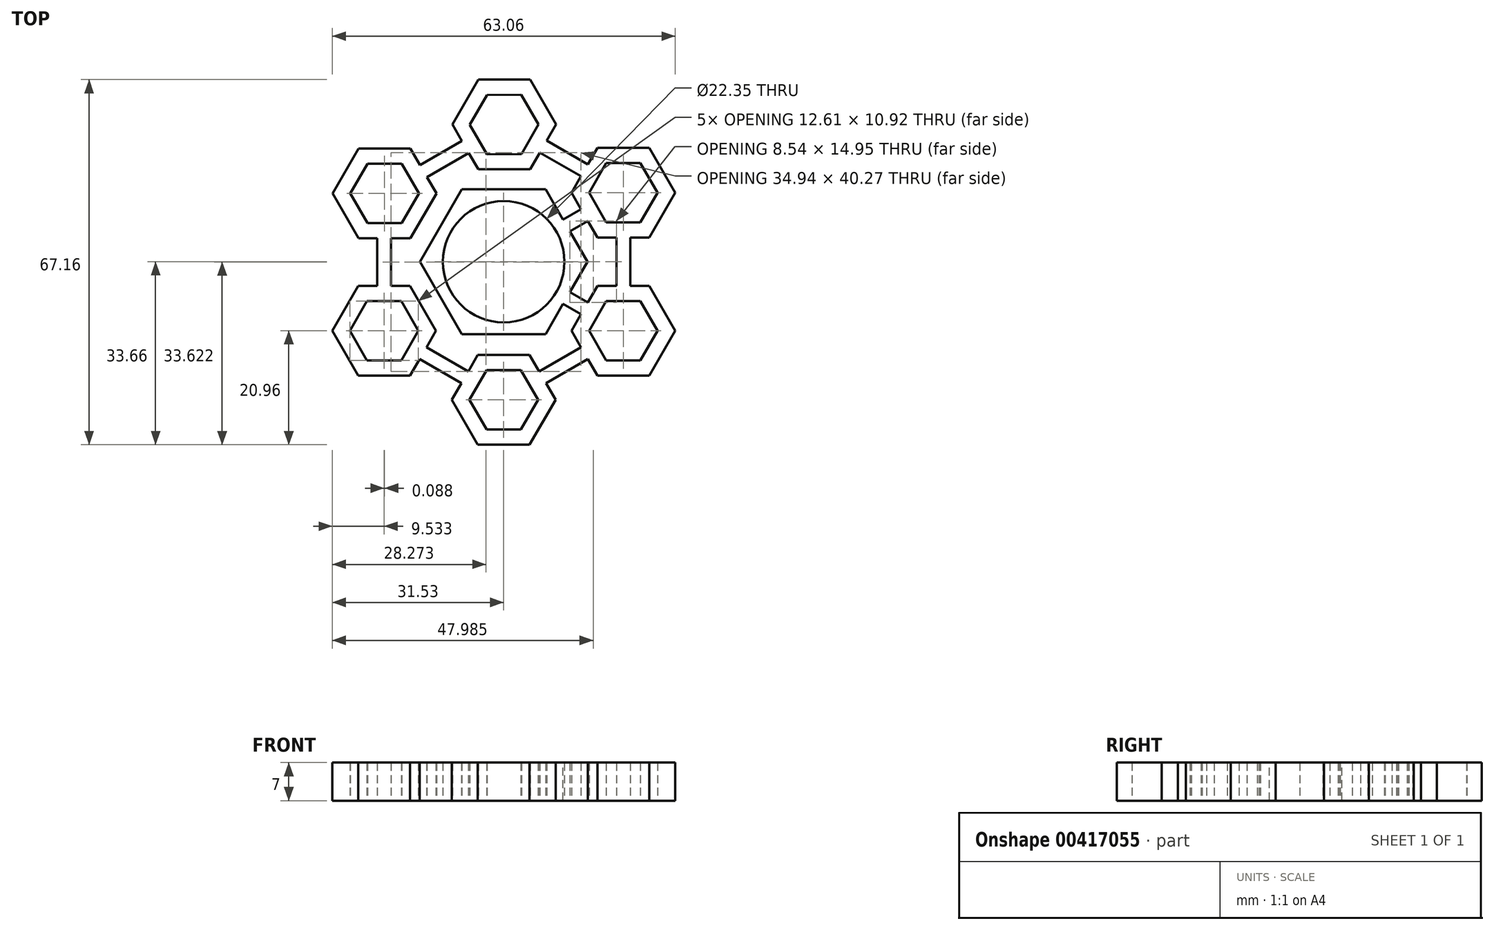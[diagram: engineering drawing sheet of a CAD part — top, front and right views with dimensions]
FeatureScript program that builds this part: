
annotation { "Feature Type Name" : "Feature", "Feature Type Description" : "" }
export const myFeature = defineFeature(function(context is Context, id is Id, definition is map)
    precondition{}
    {
        {
            var Q0;
            Q0=qCreatedBy(makeId("Top.planeOp"),FACE);
            var sketch = newSketch(context, id + "F0", { "sketchPlane" : qUnion([Q0])});
            skCircle(sketch, "E0", {"center": v(0, 0) * mm, "radius": 10.95 * mm});
            skCircle(sketch, "E1.cCircle", {"center": v(0, 0) * mm, "radius": 12.7 * mm, "construction": true});
            skLineSegment(sketch, "E1.0", {"start": v(-7.33, 12.7) * mm, "end": v(7.33, 12.7) * mm});
            skLineSegment(sketch, "E1.1", {"start": v(7.33, 12.7) * mm, "end": v(14.66, 0) * mm});
            skLineSegment(sketch, "E1.2", {"start": v(14.66, 0) * mm, "end": v(7.33, -12.7) * mm});
            skLineSegment(sketch, "E1.3", {"start": v(7.33, -12.7) * mm, "end": v(-7.33, -12.7) * mm});
            skLineSegment(sketch, "E1.4", {"start": v(-7.33, -12.7) * mm, "end": v(-14.66, 0) * mm});
            skLineSegment(sketch, "E1.5", {"start": v(-14.66, 0) * mm, "end": v(-7.33, 12.7) * mm});
            skPoint(sketch, "E1.0.midPoint", {"position": v(0, 12.7) * mm});
            skPoint(sketch, "E2.endSnap0", {"position": v(0, -12.7) * mm});
            skCircle(sketch, "E3.cCircle", {"center": v(0.09, 25.25) * mm, "radius": 5.46 * mm, "construction": true});
            skLineSegment(sketch, "E3.0", {"start": v(3.26, 19.8) * mm, "end": v(-3.05, 19.78) * mm});
            skLineSegment(sketch, "E3.1", {"start": v(-3.05, 19.78) * mm, "end": v(-6.22, 25.23) * mm});
            skLineSegment(sketch, "E3.2", {"start": v(-6.22, 25.23) * mm, "end": v(-3.08, 30.7) * mm});
            skLineSegment(sketch, "E3.3", {"start": v(-3.08, 30.7) * mm, "end": v(3.22, 30.72) * mm});
            skLineSegment(sketch, "E3.4", {"start": v(3.22, 30.72) * mm, "end": v(6.4, 25.27) * mm});
            skLineSegment(sketch, "E3.5", {"start": v(6.4, 25.27) * mm, "end": v(3.26, 19.8) * mm});
            skPoint(sketch, "E3.0.midPoint", {"position": v(0.1, 19.79) * mm});
            skCircle(sketch, "E4.cCircle", {"center": v(22, 12.7) * mm, "radius": 5.46 * mm, "construction": true});
            skLineSegment(sketch, "E4.0", {"start": v(18.84, 7.24) * mm, "end": v(15.7, 12.7) * mm});
            skLineSegment(sketch, "E4.1", {"start": v(15.7, 12.7) * mm, "end": v(18.84, 18.16) * mm});
            skLineSegment(sketch, "E4.2", {"start": v(18.84, 18.16) * mm, "end": v(25.15, 18.16) * mm});
            skLineSegment(sketch, "E4.3", {"start": v(25.15, 18.16) * mm, "end": v(28.3, 12.7) * mm});
            skLineSegment(sketch, "E4.4", {"start": v(28.3, 12.7) * mm, "end": v(25.15, 7.24) * mm});
            skLineSegment(sketch, "E4.5", {"start": v(25.15, 7.24) * mm, "end": v(18.84, 7.24) * mm});
            skPoint(sketch, "E4.0.midPoint", {"position": v(17.27, 9.97) * mm});
            skCircle(sketch, "E5.cCircle", {"center": v(22, -12.7) * mm, "radius": 5.46 * mm, "construction": true});
            skLineSegment(sketch, "E5.0", {"start": v(15.7, -12.7) * mm, "end": v(18.84, -7.24) * mm});
            skLineSegment(sketch, "E5.1", {"start": v(18.84, -7.24) * mm, "end": v(25.15, -7.24) * mm});
            skLineSegment(sketch, "E5.2", {"start": v(25.15, -7.24) * mm, "end": v(28.3, -12.7) * mm});
            skLineSegment(sketch, "E5.3", {"start": v(28.3, -12.7) * mm, "end": v(25.15, -18.16) * mm});
            skLineSegment(sketch, "E5.4", {"start": v(25.15, -18.16) * mm, "end": v(18.84, -18.16) * mm});
            skLineSegment(sketch, "E5.5", {"start": v(18.84, -18.16) * mm, "end": v(15.7, -12.7) * mm});
            skPoint(sketch, "E5.0.midPoint", {"position": v(17.27, -9.97) * mm});
            skCircle(sketch, "E6.cCircle", {"center": v(0, -25.4) * mm, "radius": 5.46 * mm, "construction": true});
            skLineSegment(sketch, "E6.0", {"start": v(-3.15, -19.94) * mm, "end": v(3.15, -19.94) * mm});
            skLineSegment(sketch, "E6.1", {"start": v(3.15, -19.94) * mm, "end": v(6.3, -25.4) * mm});
            skLineSegment(sketch, "E6.2", {"start": v(6.3, -25.4) * mm, "end": v(3.15, -30.86) * mm});
            skLineSegment(sketch, "E6.3", {"start": v(3.15, -30.86) * mm, "end": v(-3.15, -30.86) * mm});
            skLineSegment(sketch, "E6.4", {"start": v(-3.15, -30.86) * mm, "end": v(-6.3, -25.4) * mm});
            skLineSegment(sketch, "E6.5", {"start": v(-6.3, -25.4) * mm, "end": v(-3.15, -19.94) * mm});
            skPoint(sketch, "E6.0.midPoint", {"position": v(0, -19.94) * mm});
            skCircle(sketch, "E7.cCircle", {"center": v(-22, -12.7) * mm, "radius": 5.46 * mm, "construction": true});
            skLineSegment(sketch, "E7.0", {"start": v(-18.84, -7.24) * mm, "end": v(-15.7, -12.7) * mm});
            skLineSegment(sketch, "E7.1", {"start": v(-15.7, -12.7) * mm, "end": v(-18.84, -18.16) * mm});
            skLineSegment(sketch, "E7.2", {"start": v(-18.84, -18.16) * mm, "end": v(-25.15, -18.16) * mm});
            skLineSegment(sketch, "E7.3", {"start": v(-25.15, -18.16) * mm, "end": v(-28.3, -12.7) * mm});
            skLineSegment(sketch, "E7.4", {"start": v(-28.3, -12.7) * mm, "end": v(-25.15, -7.24) * mm});
            skLineSegment(sketch, "E7.5", {"start": v(-25.15, -7.24) * mm, "end": v(-18.84, -7.24) * mm});
            skPoint(sketch, "E7.0.midPoint", {"position": v(-17.27, -9.97) * mm});
            skCircle(sketch, "E8.cCircle", {"center": v(-21.9, 12.55) * mm, "radius": 5.46 * mm, "construction": true});
            skLineSegment(sketch, "E8.0", {"start": v(-15.6, 12.55) * mm, "end": v(-18.76, 7.09) * mm});
            skLineSegment(sketch, "E8.1", {"start": v(-18.76, 7.09) * mm, "end": v(-25.06, 7.09) * mm});
            skLineSegment(sketch, "E8.2", {"start": v(-25.06, 7.09) * mm, "end": v(-28.21, 12.55) * mm});
            skLineSegment(sketch, "E8.3", {"start": v(-28.21, 12.55) * mm, "end": v(-25.06, 18) * mm});
            skLineSegment(sketch, "E8.4", {"start": v(-25.06, 18) * mm, "end": v(-18.76, 18) * mm});
            skLineSegment(sketch, "E8.5", {"start": v(-18.76, 18) * mm, "end": v(-15.6, 12.55) * mm});
            skPoint(sketch, "E8.0.midPoint", {"position": v(-17.18, 9.82) * mm});
            skCircle(sketch, "E9.cCircle", {"center": v(-21.9, 12.55) * mm, "radius": 8.26 * mm, "construction": true});
            skLineSegment(sketch, "E9.0", {"start": v(-12.38, 12.55) * mm, "end": v(-17.14, 4.3) * mm});
            skLineSegment(sketch, "E9.1", {"start": v(-17.14, 4.3) * mm, "end": v(-26.67, 4.3) * mm});
            skLineSegment(sketch, "E9.2", {"start": v(-26.67, 4.3) * mm, "end": v(-31.44, 12.55) * mm});
            skLineSegment(sketch, "E9.3", {"start": v(-31.44, 12.55) * mm, "end": v(-26.67, 20.8) * mm});
            skLineSegment(sketch, "E9.4", {"start": v(-26.67, 20.8) * mm, "end": v(-17.14, 20.8) * mm});
            skLineSegment(sketch, "E9.5", {"start": v(-17.14, 20.8) * mm, "end": v(-12.38, 12.55) * mm});
            skPoint(sketch, "E9.0.midPoint", {"position": v(-14.76, 8.42) * mm});
            skCircle(sketch, "E10.cCircle", {"center": v(0.09, 25.25) * mm, "radius": 8.26 * mm, "construction": true});
            skLineSegment(sketch, "E10.0", {"start": v(4.85, 17) * mm, "end": v(-4.68, 17) * mm});
            skLineSegment(sketch, "E10.1", {"start": v(-4.68, 17) * mm, "end": v(-9.44, 25.25) * mm});
            skLineSegment(sketch, "E10.2", {"start": v(-9.44, 25.25) * mm, "end": v(-4.68, 33.5) * mm});
            skLineSegment(sketch, "E10.3", {"start": v(-4.68, 33.5) * mm, "end": v(4.85, 33.5) * mm});
            skLineSegment(sketch, "E10.4", {"start": v(4.85, 33.5) * mm, "end": v(9.62, 25.25) * mm});
            skLineSegment(sketch, "E10.5", {"start": v(9.62, 25.25) * mm, "end": v(4.85, 17) * mm});
            skPoint(sketch, "E10.0.midPoint", {"position": v(0.09, 17) * mm});
            skCircle(sketch, "E11.cCircle", {"center": v(22, 12.7) * mm, "radius": 8.26 * mm, "construction": true});
            skLineSegment(sketch, "E11.0", {"start": v(17.23, 4.45) * mm, "end": v(12.46, 12.7) * mm});
            skLineSegment(sketch, "E11.1", {"start": v(12.46, 12.7) * mm, "end": v(17.23, 20.96) * mm});
            skLineSegment(sketch, "E11.2", {"start": v(17.23, 20.96) * mm, "end": v(26.76, 20.96) * mm});
            skLineSegment(sketch, "E11.3", {"start": v(26.76, 20.96) * mm, "end": v(31.53, 12.7) * mm});
            skLineSegment(sketch, "E11.4", {"start": v(31.53, 12.7) * mm, "end": v(26.76, 4.45) * mm});
            skLineSegment(sketch, "E11.5", {"start": v(26.76, 4.45) * mm, "end": v(17.23, 4.45) * mm});
            skPoint(sketch, "E11.0.midPoint", {"position": v(14.85, 8.57) * mm});
            skCircle(sketch, "E12.cCircle", {"center": v(22, -12.7) * mm, "radius": 8.26 * mm, "construction": true});
            skLineSegment(sketch, "E12.0", {"start": v(12.46, -12.7) * mm, "end": v(17.23, -4.44) * mm});
            skLineSegment(sketch, "E12.1", {"start": v(17.23, -4.45) * mm, "end": v(26.76, -4.44) * mm});
            skLineSegment(sketch, "E12.2", {"start": v(26.76, -4.44) * mm, "end": v(31.53, -12.7) * mm});
            skLineSegment(sketch, "E12.3", {"start": v(31.53, -12.7) * mm, "end": v(26.76, -20.96) * mm});
            skLineSegment(sketch, "E12.4", {"start": v(26.76, -20.96) * mm, "end": v(17.23, -20.96) * mm});
            skLineSegment(sketch, "E12.5", {"start": v(17.23, -20.96) * mm, "end": v(12.46, -12.7) * mm});
            skPoint(sketch, "E12.0.midPoint", {"position": v(14.85, -8.57) * mm});
            skCircle(sketch, "E13.cCircle", {"center": v(0, -25.4) * mm, "radius": 8.26 * mm, "construction": true});
            skLineSegment(sketch, "E13.0", {"start": v(-4.77, -17.14) * mm, "end": v(4.77, -17.14) * mm});
            skLineSegment(sketch, "E13.1", {"start": v(4.77, -17.15) * mm, "end": v(9.53, -25.4) * mm});
            skLineSegment(sketch, "E13.2", {"start": v(9.53, -25.4) * mm, "end": v(4.77, -33.65) * mm});
            skLineSegment(sketch, "E13.3", {"start": v(4.77, -33.65) * mm, "end": v(-4.77, -33.66) * mm});
            skLineSegment(sketch, "E13.4", {"start": v(-4.77, -33.66) * mm, "end": v(-9.53, -25.4) * mm});
            skLineSegment(sketch, "E13.5", {"start": v(-9.53, -25.4) * mm, "end": v(-4.77, -17.15) * mm});
            skPoint(sketch, "E13.0.midPoint", {"position": v(0, -17.14) * mm});
            skCircle(sketch, "E14.cCircle", {"center": v(-22, -12.7) * mm, "radius": 8.26 * mm, "construction": true});
            skLineSegment(sketch, "E14.0", {"start": v(-17.23, -4.45) * mm, "end": v(-12.46, -12.7) * mm});
            skLineSegment(sketch, "E14.1", {"start": v(-12.46, -12.7) * mm, "end": v(-17.23, -20.96) * mm});
            skLineSegment(sketch, "E14.2", {"start": v(-17.23, -20.96) * mm, "end": v(-26.76, -20.96) * mm});
            skLineSegment(sketch, "E14.3", {"start": v(-26.76, -20.96) * mm, "end": v(-31.53, -12.7) * mm});
            skLineSegment(sketch, "E14.4", {"start": v(-31.53, -12.7) * mm, "end": v(-26.76, -4.45) * mm});
            skLineSegment(sketch, "E14.5", {"start": v(-26.76, -4.45) * mm, "end": v(-17.23, -4.45) * mm});
            skPoint(sketch, "E14.0.midPoint", {"position": v(-14.85, -8.57) * mm});
            skLineSegment(sketch, "E15", {"start": v(-6.43, 20.02) * mm, "end": v(-14.12, 15.57) * mm});
            skLineSegment(sketch, "E16", {"start": v(-14.21, 15.73) * mm, "end": v(-15.4, 17.77) * mm});
            skLineSegment(sketch, "E17", {"start": v(-15.4, 17.77) * mm, "end": v(-7.7, 22.22) * mm});
            skLineSegment(sketch, "E18", {"start": v(-23.27, 4.3) * mm, "end": v(-23.27, -4.45) * mm});
            skLineSegment(sketch, "E19", {"start": v(-23.27, -4.45) * mm, "end": v(-20.73, -4.45) * mm});
            skLineSegment(sketch, "E20", {"start": v(-20.73, -4.45) * mm, "end": v(-20.73, 4.3) * mm});
            skLineSegment(sketch, "E21", {"start": v(-15.48, -17.93) * mm, "end": v(-7.78, -22.37) * mm});
            skLineSegment(sketch, "E22", {"start": v(-7.78, -22.37) * mm, "end": v(-6.51, -20.17) * mm});
            skLineSegment(sketch, "E23", {"start": v(-6.51, -20.17) * mm, "end": v(-14.21, -15.73) * mm});
            skLineSegment(sketch, "E24", {"start": v(6.51, -20.17) * mm, "end": v(14.21, -15.73) * mm});
            skLineSegment(sketch, "E25", {"start": v(14.21, -15.73) * mm, "end": v(15.48, -17.93) * mm});
            skLineSegment(sketch, "E26", {"start": v(15.48, -17.93) * mm, "end": v(7.7, -22.42) * mm});
            skLineSegment(sketch, "E27", {"start": v(20.73, -4.45) * mm, "end": v(20.73, 4.45) * mm});
            skLineSegment(sketch, "E28", {"start": v(20.73, 4.45) * mm, "end": v(23.27, 4.45) * mm});
            skLineSegment(sketch, "E29", {"start": v(23.27, 4.45) * mm, "end": v(23.27, -4.54) * mm});
            skLineSegment(sketch, "E30", {"start": v(14.21, 15.73) * mm, "end": v(6.65, 20.1) * mm});
            skLineSegment(sketch, "E31", {"start": v(6.65, 20.1) * mm, "end": v(7.92, 22.3) * mm});
            skLineSegment(sketch, "E32", {"start": v(7.92, 22.3) * mm, "end": v(15.48, 17.93) * mm});
            skLineSegment(sketch, "E33.bottom", {"start": v(-1.27, -12.7) * mm, "end": v(1.27, -12.7) * mm});
            skLineSegment(sketch, "E33.top", {"start": v(-1.27, -17.14) * mm, "end": v(1.27, -17.14) * mm});
            skLineSegment(sketch, "E34.bottom", {"start": v(1.27, 12.7) * mm, "end": v(-1.27, 12.7) * mm});
            skLineSegment(sketch, "E34.top", {"start": v(1.27, 17) * mm, "end": v(-1.27, 17) * mm});
            skLineSegment(sketch, "E35", {"start": v(14.21, 9.67) * mm, "end": v(10.3, 7.42) * mm});
            skLineSegment(sketch, "E36", {"start": v(10.3, 7.42) * mm, "end": v(11.63, 5.25) * mm});
            skLineSegment(sketch, "E37", {"start": v(11.63, 5.25) * mm, "end": v(15.48, 7.47) * mm});
            skLineSegment(sketch, "E38", {"start": v(15.48, -7.47) * mm, "end": v(11.58, -5.22) * mm});
            skLineSegment(sketch, "E39", {"start": v(11.58, -5.22) * mm, "end": v(10.36, -7.45) * mm});
            skLineSegment(sketch, "E40", {"start": v(10.36, -7.45) * mm, "end": v(14.21, -9.67) * mm});
            skLineSegment(sketch, "E41", {"start": v(-10.36, -7.45) * mm, "end": v(-14.21, -9.67) * mm});
            skLineSegment(sketch, "E42", {"start": v(-14.21, -9.67) * mm, "end": v(-15.48, -7.47) * mm});
            skLineSegment(sketch, "E43", {"start": v(-15.48, -7.47) * mm, "end": v(-11.63, -5.25) * mm});
            skLineSegment(sketch, "E44", {"start": v(-11.63, 5.25) * mm, "end": v(-15.35, 7.4) * mm});
            skLineSegment(sketch, "E45", {"start": v(-15.35, 7.4) * mm, "end": v(-14.08, 9.6) * mm});
            skLineSegment(sketch, "E46", {"start": v(-14.08, 9.6) * mm, "end": v(-10.36, 7.45) * mm});
            skLineSegment(sketch, "E47", {"start": v(-11.63, 5.25) * mm, "end": v(-10.36, 7.45) * mm});
            skLineSegment(sketch, "E48", {"start": v(-14.08, 9.6) * mm, "end": v(-15.35, 7.4) * mm});
            skLineSegment(sketch, "E49", {"start": v(15.48, 7.47) * mm, "end": v(14.21, 9.67) * mm});
            skLineSegment(sketch, "E50", {"start": v(-11.63, -5.25) * mm, "end": v(-15.48, -7.47) * mm});
            skLineSegment(sketch, "E51", {"start": v(-15.48, -7.47) * mm, "end": v(-14.21, -9.67) * mm});
            skLineSegment(sketch, "E52", {"start": v(-14.21, -9.67) * mm, "end": v(-10.36, -7.45) * mm});
            skLineSegment(sketch, "E53", {"start": v(-10.36, -7.45) * mm, "end": v(-11.63, -5.25) * mm});
            skCircle(sketch, "E54", {"center": v(0, 0) * mm, "radius": 11.08 * mm});
            skCircle(sketch, "E55", {"center": v(0, 0) * mm, "radius": 11.07 * mm});
            skSolve(sketch);
        }
        {
            var Q0;
            Q0 = qSketchRegion(id + "F0", true);
            var Q1;
            Q1=makeQuery(id+"F0.imprint","IMPRINT",FACE,{"disambiguationData":[TD([[makeQuery(id+"F0.imprint","IMPRINT",EDGE,{"derivedFrom":sQuery(id+"F0.wireOp",EDGE,"E34.bottom")}),-1.0]])]});
            var Q2;
            Q2=makeQuery(id+"F0.imprint","IMPRINT",FACE,{"disambiguationData":[TD([[makeQuery(id+"F0.imprint","IMPRINT",EDGE,{"derivedFrom":sQuery(id+"F0.wireOp",EDGE,"E50")}),1.0]])]});
            var Q3;
            Q3=makeQuery(id+"F0.imprint","IMPRINT",FACE,{"disambiguationData":[TD([[makeQuery(id+"F0.imprint","IMPRINT",EDGE,{"derivedFrom":sQuery(id+"F0.wireOp",EDGE,"E33.bottom")}),-1.0]])]});
            var Q4;
            {var subQ0=sQuery(id+"F0.wireOp",EDGE,"E40");Q4=makeQuery(id+"F0.imprint","IMPRINT",FACE,{"disambiguationData":[TD([[makeQuery(id+"F0.imprint","IMPRINT",EDGE,{"derivedFrom":subQ0}),1.0]])]});}
            var Q5;
            {var subQ0=sQuery(id+"F0.wireOp",EDGE,"E37");Q5=makeQuery(id+"F0.imprint","IMPRINT",FACE,{"disambiguationData":[TD([[makeQuery(id+"F0.imprint","IMPRINT",EDGE,{"derivedFrom":subQ0}),1.0]])]});}
            var Q6;
            Q6=makeQuery(id+"F0.imprint","IMPRINT",FACE,{"disambiguationData":[TD([[makeQuery(id+"F0.imprint","IMPRINT",EDGE,{"derivedFrom":sQuery(id+"F0.wireOp",EDGE,"E46")}),-1.0]])]});
            extrude(context, id + "F1", {"entities" : qUnion([Q0, Q1, Q2, Q3, Q4, Q5, Q6]), "depth" : 7 * mm});
        }
        {
            var Q0;
            Q0=qCreatedBy(makeId("Top.planeOp"),FACE);
            var sketch = newSketch(context, id + "F2", { "sketchPlane" : qUnion([Q0])});
            skCircle(sketch, "E56", {"center": v(0, 0) * mm, "radius": 11.18 * mm});
            skCircle(sketch, "E57.cCircle", {"center": v(0, 0) * mm, "radius": 13.34 * mm, "construction": true});
            skLineSegment(sketch, "E57.0", {"start": v(-7.7, 13.33) * mm, "end": v(7.7, 13.34) * mm});
            skLineSegment(sketch, "E57.1", {"start": v(7.7, 13.34) * mm, "end": v(15.4, 0) * mm});
            skLineSegment(sketch, "E57.2", {"start": v(15.4, 0) * mm, "end": v(7.7, -13.33) * mm});
            skLineSegment(sketch, "E57.3", {"start": v(7.7, -13.33) * mm, "end": v(-7.7, -13.34) * mm});
            skLineSegment(sketch, "E57.4", {"start": v(-7.7, -13.34) * mm, "end": v(-15.4, 0) * mm});
            skLineSegment(sketch, "E57.5", {"start": v(-15.4, 0) * mm, "end": v(-7.7, 13.33) * mm});
            skPoint(sketch, "E57.0.midPoint", {"position": v(0, 13.33) * mm});
            skSolve(sketch);
        }
        {
            var Q0;
            Q0 = qSketchRegion(id + "F2", true);
            extrude(context, id + "F3", {"entities" : qUnion([Q0]), "operationType" : NewBodyOperationType.ADD, "depth" : 7 * mm});
        }
    });
